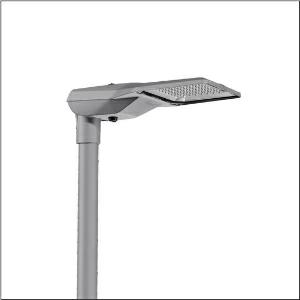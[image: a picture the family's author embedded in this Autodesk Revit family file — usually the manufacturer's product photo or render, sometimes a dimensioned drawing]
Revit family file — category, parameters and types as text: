
# Revit family: streetlight_sl_21_midi___st0_5a_5xe3b33t08nb_f8ff
name_source: partatom
category: Lighting Fixtures
units: mm (PartAtom-declared; Revit-internal decimal feet)

## family parameters
Cut with Voids When Loaded = No
Host = Face
Light Source = No
Part Type = Normal
Room Calculation Point = No
Round Connector Dimension = Use Diameter
Shared = No

## types (1)
- --- (1 x LED, 22700 lm, 151.2 W, 3000K)
    Apparent Load = 151 VA
    CIE Flux Codes = 43 76 97 100 100
    Color Rendering = 70
    Color Temperature = 3000K
    Default Elevation = 1800 mm
    Description = Streetlight SL 21 midi, mast luminaire, primary light control with lens, of PMMA, primary optical cover: cover, of toughened safety glass, transparent, light distribution: ST0.5a, light emission: direct distribution, primary light characteristic: asymmetric, installation type: side-entry, post-top, LED, High Power LED, rated luminous flux: 22.700lm, luminous efficacy: 150lm/W, light colour: 730, colour temperature: 3000K, control: overheat protection, constant luminous flux control, time-dependent luminous flux control, flexible luminous flux parameterisation, presetting dimming logarithmic, mains connection: 230..240V, AC, 50/60Hz, start of lifetime: 151W, end of service life: 157W, reduction: 70W, luminaire housing, of diecast aluminium, powder-coated, Siteco® metallic grey (DB 702S), corrosivity category C5 mid according to DIN EN ISO 12944, please order mast flange separately, inclination adjustable: 0°, 5°, 10°, 15°, sealing non-destructively replaceable, multi-level sealing system, length: 644mm, width: 335mm, height: 110mm, mast flange for spigot size: 42mm (side-entry): 5XC10008XM4, 60/48mm (side-entry/post-top): 5XC10108XM2, 76/60mm (side-entry/post-top): 5XC10108XM1, Smart Interface below and above, protection rating (complete): IP66, insulation class (complete): insulation class II (safety insulation), certification: CE, ENEC, ENEC+, VDE, impact resistance: IK09, permissible operating ambient temperature for outdoor applications: -40..+50°C, standard-compliant lighting for roads and squares, packaging unit: 1 piece

Light Distribution: ST0.5a
    Height = 111 mm
    Lamp = 1 x LED
    Lamp Light Flux = 22700 lm
    Lamp Power = 151.2 W
    Lamp count = 1
    Length = 644 mm
    Luminous efficacy = 150 lm/W
    Manufacturer = Siteco
    ModVariant = No
    Model = 5XE3B33T08NB
    Number of Poles = 1
    OnlyDefault = Yes
    Power Factor = 1
    Product Name = Streetlight SL 21 midi | ST0.5a
    Product group = mast luminaire | pylon top
    ProductGroupID = 6100
    Protection Class = Protection class II
    Protection Degree = IP 66
    RLX_Detail_Level = 1
    RLX_Emergency_Light_Flux = 0 lm
    RLX_Emergency_Type = 0
    RLX_Emergency_Type_DB = No
    RlxData = <blob elided: 102113 chars, md5=af864841>
    Socket = socket
    Standby Power = 0 W
    System Light Flux = 22700 lm
    System Power = 151 W
    Type Comments = factory setting: luminous flux: 100 % | dim-lin: 254 | 802 mA
    Type Image = l_1004304.jpg
    URL = http://relux.com
    VarID = @adj_122127
    Voltage = 0 V
    Weight = 0.00 kg
    Width = 336 mm

## geometry (parser evidence)
native form markers: Blend x4, Sweep x10
no freeform markers — native parametric forms only
